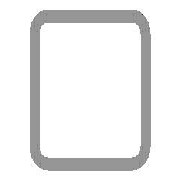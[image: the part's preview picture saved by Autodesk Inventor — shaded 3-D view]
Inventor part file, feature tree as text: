
AUTODESK INVENTOR PART (.ipt)
format: ipt  version: 2025 (Build 290162010, 162A)  size: 133,120 bytes
history: native  units: mm (DEFAULTED — no unit token found)
features: other x4, sketch x1, plane x1
ambient origin geometry x8: Origin, YZ Plane, XZ Plane, XY Plane, X Axis, Y Axis, Z Axis, Center Point
bodies: Solid1 (feature_tree), Body (feature_tree)
feature tree (6):
  parser-record x1  (decoder bookkeeping rows leaked as tree rows — omitted from the tree; the rows remain in map.json)
  other  "Driven Length"
  other  "Start Plane"
  other  "End Plane"
  sketch  "Sketch3"  dims[d3=1800.0mm d4=0.0mm d7=4.0mm d9=40.0mm d11=40.0mm d12=2.0mm d13=-0.0mm d14=1800.0mm d15=20.0mm d16=20.0mm d17=90.0deg d18=1800.0mm]
  plane  "Work Plane3"
